AUTODESK INVENTOR PART (.ipt)
format: ipt  version: 2021 (Build 250183000, 183)  size: 370,176 bytes
history: native  units: mm
features: extrude x12, other x10, fillet x9, projected_geometry x1
ambient origin geometry x8: Origin, YZ Plane, XZ Plane, XY Plane, X Axis, Y Axis, Z Axis, Center Point
bodies: Solid1 (feature_tree)
feature tree (32):
  other  "base_sketch"
  extrude  "mount"  Depth=3.1mm
  extrude  "plate"  Depth=3.1mm
  extrude  "sides_wall"  Depth=3.1mm
  extrude  "sides_cutout"  Depth=17.177mm
  extrude  "side_clip_left"  Depth=6.0mm
  extrude  "side_clip_right"  Depth=6.0mm
  other  "end_clip_left_sketch"
  other  "end_clip_right_sketch"
  extrude  "end_clip_left"  Depth=14.823mm
  extrude  "end_clip_right"  TaperAngle=150.0deg  [1 undecoded]
  fillet  "clips"  [1 undecoded]
  fillet  "side_smooth"  Radius=40.0mm
  extrude  "end_clip_narrow_left"  Depth=20.0mm
  extrude  "end_clip_narrow_right"  Depth=6.0mm
  fillet  "narrow_smooth"  Radius=4.0mm
  fillet  "inside_fillet"  Radius=3.0mm
  extrude  "control_wire_inlay"  Depth=8.0mm
  fillet  "control_wire_inlay_to_inside"  Radius=32.5mm
  fillet  "plate_end"  Radius=33.2mm
  fillet  "outside"  Radius=6.0mm
  extrude  "wire_ramp"  Depth=2.0mm TaperAngle=0.0deg
  fillet  "bottom_inside"  Radius=23.2mm
  fillet  "Fillet12"  Radius=10.0mm
  other  "sides_cutout_sketch"
  other  "side_clip_left_sketch"
  other  "side_clip_right_sketch"
  other  "end_clip_narrow_left_sketch"
  other  "end_clip_narrow_right_sketch"
  projected_geometry  "Projected Loop1"
  other  "control_wire_inlay_sketch"
  other  "wire_ramp_sketch"
note: 2 required parameter values undecoded (feature->parameter linkage not recoverable at this tier; creation-order binding heuristic only, values carry confidence <= 0.55)
